# Revit family: QF_ELECTROLUXPROFESSIONAL_1L0A45_WE170V_E
name_source: partatom
category: Attrezzature speciali
units: mm (PartAtom-declared; Revit-internal decimal feet)

## family parameters
Basato su piano di lavoro = No
Condiviso = No
Punto di calcolo locali = No
Quota connettore circolare = Usa diametro
Sempre verticale = Sì
Taglio con vuoti quando caricato = No
Tipo di parte = Normale

## types (4) — shared parameters
Depth = 620 mm
Depth Actual = 624 mm
Height = 847 mm
Height Actual = 850 mm
Latent Heat Output = 0.0
Length Actual = 597 mm
Modello = WE170V
Phase = 1
Produttore = Electrolux Professional
Sensible Heat Output = 0.0
URL = www.electroluxprofessional.com
Weight = 80.5
Width = 597 mm
zero-valued in all types: Gas KW, Prospetto di default, Steam Pounds per Hour

## per-type parameters (varying)
| type | Cycle | Descrizione | Item Number | Volts | Watts |
| 914535406 | 60 Hz | myPRO SMART PROFESSIONAL WASHER WE170V 8KG VALVE 200/60/1N 2,2KW JP SST/DARK BLUE | 1L0BJN | 200 V | 1700 W |
| 914535413 | 50 Hz | myPRO SMART PROFESSIONAL WASHER WE170V 8KG VALVE 230-240/50/1N 2,2KW EN PLUG-UK SST/DARK BLUE | 1LSP98 | 230 V | 2200 W |
| 914535414 | 50 Hz | myPRO SMART PROFESSIONAL WASHER WE170V 8KG VALVE 230-240/50/1N 2,2KW DE SCHUKO SST/DARK BLUE | 1LSP99 | 230 V | 2200 W |
| 914535416 | 50 Hz | myPRO SMART PROFESSIONAL WASHER WE170V 8KG VALVE 230-240/50/1N 2,2KW SYMBOLS SCHUKO SST/DARK BLUE | 1LSP9B | 230 V | 2200 W |

## geometry (parser evidence)
native form markers: Sweep x2
no freeform markers — native parametric forms only
